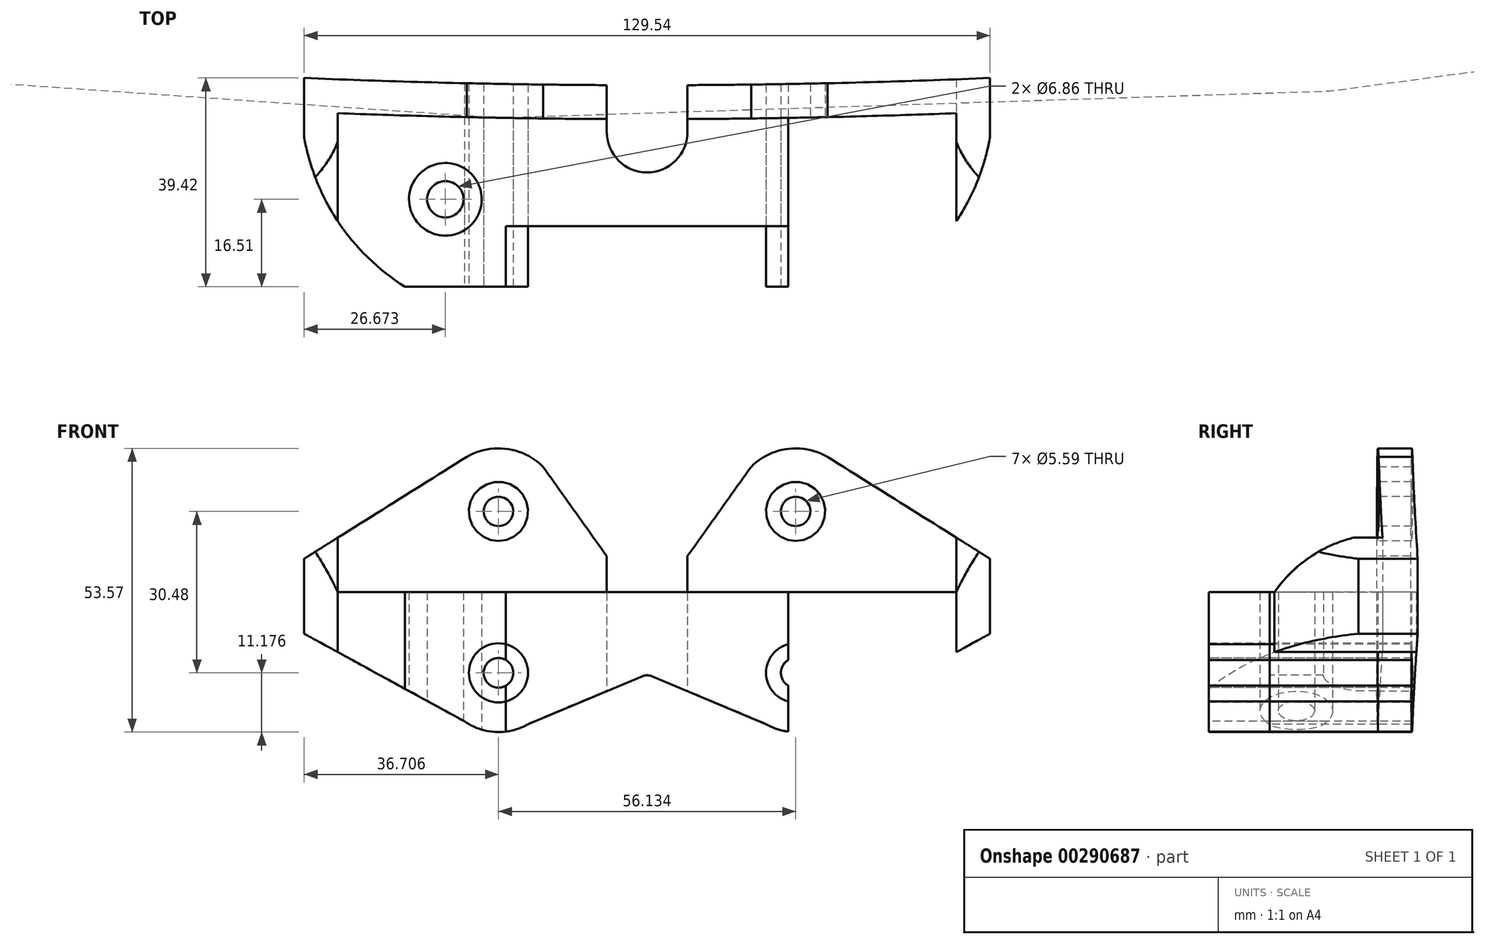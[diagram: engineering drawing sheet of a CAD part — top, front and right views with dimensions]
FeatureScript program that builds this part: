
annotation { "Feature Type Name" : "Feature", "Feature Type Description" : "" }
export const myFeature = defineFeature(function(context is Context, id is Id, definition is map)
    precondition{}
    {
        {
            var Q0;
            Q0=qCreatedBy(makeId("Top.planeOp"),FACE);
            var sketch = newSketch(context, id + "F0", { "sketchPlane" : qUnion([Q0])});
            skLineSegment(sketch, "E0", {"start": v(-442.16, 137.19) * mm, "end": v(-442.16, -137.19) * mm, "construction": true});
            skLineSegment(sketch, "E1.bottom", {"start": v(-353.26, -20.32) * mm, "end": v(-531.06, -20.32) * mm});
            skLineSegment(sketch, "E1.top", {"start": v(-353.26, 20.32) * mm, "end": v(-531.06, 20.32) * mm});
            skLineSegment(sketch, "E1.left", {"start": v(-353.26, -20.32) * mm, "end": v(-353.26, 20.32) * mm});
            skLineSegment(sketch, "E1.right", {"start": v(-531.06, -20.32) * mm, "end": v(-531.06, 20.32) * mm});
            skPoint(sketch, "E1.middle", {"position": v(-442.16, 0) * mm});
            skPoint(sketch, "E1.middle.positionSnap0", {"position": v(-442.16, 0) * mm});
            skPoint(sketch, "E1.centerSnap0", {"position": v(-442.16, 0) * mm});
            skArc(sketch, "E2", {"start": v(-531.06, 20.32) * mm, "mid": v(-442.16, 17.73) * mm, "end": v(-353.26, 20.32) * mm});
            skLineSegment(sketch, "E3", {"start": v(-500.58, -20.32) * mm, "end": v(-500.58, 12.45) * mm});
            skLineSegment(sketch, "E4", {"start": v(-383.74, -20.32) * mm, "end": v(-383.74, 12.45) * mm});
            skArc(sketch, "E5", {"start": v(-500.58, 12.45) * mm, "mid": v(-442.16, 11.33) * mm, "end": v(-383.74, 12.45) * mm});
            skLineSegment(sketch, "E6", {"start": v(-468.83, -20.32) * mm, "end": v(-468.83, -8.9) * mm});
            skLineSegment(sketch, "E7", {"start": v(-468.83, -8.9) * mm, "end": v(-415.49, -8.9) * mm});
            skLineSegment(sketch, "E8", {"start": v(-415.49, -8.9) * mm, "end": v(-415.49, -20.32) * mm});
            skCircle(sketch, "E9", {"center": v(-442.16, 8.89) * mm, "radius": 7.62 * mm});
            skLineSegment(sketch, "E10", {"start": v(-480.26, -3.81) * mm, "end": v(-404.06, -3.81) * mm, "construction": true});
            skCircle(sketch, "E11", {"center": v(-480.26, -3.81) * mm, "radius": 3.43 * mm});
            skCircle(sketch, "E12", {"center": v(-404.06, -3.81) * mm, "radius": 3.43 * mm});
            skLineSegment(sketch, "E13", {"start": v(-434.54, 20.32) * mm, "end": v(-434.54, 8.89) * mm});
            skLineSegment(sketch, "E14", {"start": v(-449.78, 20.32) * mm, "end": v(-449.78, 8.89) * mm});
            skCircle(sketch, "E15", {"center": v(-480.26, -3.81) * mm, "radius": 6.86 * mm});
            skCircle(sketch, "E16", {"center": v(-404.06, -3.81) * mm, "radius": 6.86 * mm});
            skSolve(sketch);
        }
        {
            var Q0;
            Q0=sQuery(id+"F0.wireOp",EDGE,"E1.bottom");
            var Q1;
            Q1=qCreatedBy(makeId("Front.planeOp"),FACE);
            cPlane(context, id + "F1", {"entities" : qUnion([Q0, Q1]), "cplaneType" : CPlaneType.LINE_ANGLE, "offset" : 25.4 * mm, "angle" : 0 * degree, "width" : 152.4 * mm, "height" : 152.4 * mm});
        }
        {
            var Q0;
            Q0=qCreatedBy(id+"F1.planeOp",FACE);
            var sketch = newSketch(context, id + "F2", { "sketchPlane" : qUnion([Q0])});
            skLineSegment(sketch, "E17", {"start": v(531.06, 0) * mm, "end": v(353.26, 0) * mm, "construction": true});
            skLineSegment(sketch, "E18.bottom", {"start": v(414.09, 44.2) * mm, "end": v(470.22, 44.2) * mm, "construction": true});
            skLineSegment(sketch, "E18.top", {"start": v(414.09, 13.72) * mm, "end": v(470.22, 13.72) * mm, "construction": true});
            skLineSegment(sketch, "E18.left", {"start": v(414.09, 44.2) * mm, "end": v(414.09, 13.72) * mm, "construction": true});
            skLineSegment(sketch, "E18.right", {"start": v(470.22, 44.2) * mm, "end": v(470.22, 13.72) * mm, "construction": true});
            skPoint(sketch, "E18.middle", {"position": v(442.16, 28.96) * mm});
            skLineSegment(sketch, "E19", {"start": v(407.26, 28.96) * mm, "end": v(380.42, 28.96) * mm, "construction": true});
            skCircle(sketch, "E20", {"center": v(414.09, 13.72) * mm, "radius": 2.8 * mm});
            skCircle(sketch, "E21", {"center": v(414.09, 44.2) * mm, "radius": 2.8 * mm});
            skCircle(sketch, "E22", {"center": v(470.22, 44.2) * mm, "radius": 2.8 * mm});
            skCircle(sketch, "E23", {"center": v(470.22, 13.72) * mm, "radius": 2.8 * mm});
            skCircle(sketch, "E24", {"center": v(470.22, 13.72) * mm, "radius": 5.59 * mm});
            skCircle(sketch, "E25", {"center": v(470.22, 44.2) * mm, "radius": 5.59 * mm});
            skCircle(sketch, "E26", {"center": v(414.09, 44.2) * mm, "radius": 5.59 * mm});
            skCircle(sketch, "E27", {"center": v(414.09, 13.72) * mm, "radius": 5.59 * mm});
            skLineSegment(sketch, "E28", {"start": v(531.06, 0) * mm, "end": v(531.06, 80.01) * mm, "construction": true});
            skSolve(sketch);
        }
        {
            var Q0;
            {var subQ2=sQuery(id+"F0.wireOp",EDGE,"E1.right");Q0=makeQuery(id+"F0.imprint","IMPRINT",FACE,{"disambiguationData":[TD([[makeQuery(id+"F0.imprint","IMPRINT",EDGE,{"derivedFrom":subQ2}),-1.0]])]});}
            var Q1;
            {var subQ2=sQuery(id+"F0.wireOp",EDGE,"E1.left");Q1=makeQuery(id+"F0.imprint","IMPRINT",FACE,{"disambiguationData":[TD([[makeQuery(id+"F0.imprint","IMPRINT",EDGE,{"derivedFrom":subQ2}),1.0]])]});}
            var Q2;
            Q2=sQuery(id+"F2.wireOp",VERTEX,"E28.end");
            extrude(context, id + "F3", {"entities" : qUnion([Q0, Q1]), "endBound" : BoundingType.UP_TO_VERTEX, "endBoundEntityVertex" : qUnion([Q2]), "depth" : 25.4 * mm});
        }
        {
            var Q0;
            {var subQ10=sQuery(id+"F0.wireOp",EDGE,"E3");Q0=makeQuery(id+"F0.imprint","IMPRINT",FACE,{"disambiguationData":[TD([[makeQuery(id+"F0.imprint","IMPRINT",EDGE,{"derivedFrom":subQ10}),-1.0]])]});}
            var Q1;
            Q1=makeQuery(id+"F0.imprint","IMPRINT",FACE,{"disambiguationData":[TD([[makeQuery(id+"F0.imprint","IMPRINT",EDGE,{"derivedFrom":sQuery(id+"F0.wireOp",EDGE,"E11")}),-1.0]])]});
            var Q2;
            Q2=makeQuery(id+"F0.imprint","IMPRINT",FACE,{"disambiguationData":[TD([[makeQuery(id+"F0.imprint","IMPRINT",EDGE,{"derivedFrom":sQuery(id+"F0.wireOp",EDGE,"E12")}),-1.0]])]});
            var Q3;
            Q3=sQuery(id+"F2.wireOp",VERTEX,"E19.start");
            extrude(context, id + "F4", {"entities" : qUnion([Q0, Q1, Q2]), "endBound" : BoundingType.UP_TO_VERTEX, "endBoundEntityVertex" : qUnion([Q3]), "depth" : 25.4 * mm});
        }
        {
            var Q0;
            Q0=makeQuery(id+"F2.imprint","IMPRINT",FACE,{"disambiguationData":[TD([[makeQuery(id+"F2.imprint","IMPRINT",EDGE,{"derivedFrom":sQuery(id+"F2.wireOp",EDGE,"E22")}),1.0]])]});
            var Q1;
            Q1=makeQuery(id+"F2.imprint","IMPRINT",FACE,{"disambiguationData":[TD([[makeQuery(id+"F2.imprint","IMPRINT",EDGE,{"derivedFrom":sQuery(id+"F2.wireOp",EDGE,"E23")}),1.0]])]});
            var Q2;
            Q2=makeQuery(id+"F2.imprint","IMPRINT",FACE,{"disambiguationData":[TD([[makeQuery(id+"F2.imprint","IMPRINT",EDGE,{"derivedFrom":sQuery(id+"F2.wireOp",EDGE,"E21")}),1.0]])]});
            var Q3;
            Q3=makeQuery(id+"F2.imprint","IMPRINT",FACE,{"disambiguationData":[TD([[makeQuery(id+"F2.imprint","IMPRINT",EDGE,{"derivedFrom":sQuery(id+"F2.wireOp",EDGE,"E20")}),1.0]])]});
            extrude(context, id + "F5", {"entities" : qUnion([Q0, Q1, Q2, Q3]), "operationType" : NewBodyOperationType.REMOVE, "endBound" : BoundingType.THROUGH_ALL, "depth" : 25.4 * mm});
        }
        {
            var Q0;
            Q0=makeQuery(id+"F2.imprint","IMPRINT",FACE,{"disambiguationData":[TD([[makeQuery(id+"F2.imprint","IMPRINT",EDGE,{"derivedFrom":sQuery(id+"F2.wireOp",EDGE,"E22")}),-1.0]])]});
            var Q1;
            Q1=makeQuery(id+"F2.imprint","IMPRINT",FACE,{"disambiguationData":[TD([[makeQuery(id+"F2.imprint","IMPRINT",EDGE,{"derivedFrom":sQuery(id+"F2.wireOp",EDGE,"E21")}),-1.0]])]});
            var Q2;
            {var subQ0=sQuery(id+"F0.wireOp",EDGE,"E2");Q2=makeQuery(id+"F3.opExtrude","SWEPT_FACE",FACE,{"disambiguationData":[OSD([subQ0]),TDD([makeQuery(id+"F0.imprint","IMPRINT",EDGE,{"disambiguationData":[TD([[makeQuery(id+"F0.imprint","INTERSECT",VERTEX,{"derivedFrom":[subQ0,sQuery(id+"F0.wireOp",EDGE,"E14")]}),1.0]])],"derivedFrom":subQ0})])]});}
            var Q3;
            {var subQ0=sQuery(id+"F0.wireOp",EDGE,"E5");Q3=makeQuery(id+"F3.opExtrude","SWEPT_FACE",FACE,{"disambiguationData":[OSD([subQ0]),TDD([makeQuery(id+"F0.imprint","IMPRINT",EDGE,{"disambiguationData":[TD([[makeQuery(id+"F0.imprint","INTERSECT",VERTEX,{"derivedFrom":[sQuery(id+"F0.wireOp",EDGE,"E3"),subQ0]}),-1.0]])],"derivedFrom":subQ0})])]});}
            extrude(context, id + "F6", {"entities" : qUnion([Q0, Q1]), "endBound" : BoundingType.UP_TO_SURFACE, "endBoundEntityFace" : qUnion([Q2]), "depth" : 25.4 * mm, "hasSecondDirection" : true, "secondDirectionBound" : SecondDirectionBoundingType.UP_TO_SURFACE, "secondDirectionOppositeDirection" : false, "secondDirectionBoundEntityFace" : qUnion([Q3]), "secondDirectionDepth" : 25.4 * mm});
        }
        {
            var Q0;
            Q0=makeQuery(id+"F2.imprint","IMPRINT",FACE,{"disambiguationData":[TD([[makeQuery(id+"F2.imprint","IMPRINT",EDGE,{"derivedFrom":sQuery(id+"F2.wireOp",EDGE,"E23")}),-1.0]])]});
            var Q1;
            Q1=makeQuery(id+"F2.imprint","IMPRINT",FACE,{"disambiguationData":[TD([[makeQuery(id+"F2.imprint","IMPRINT",EDGE,{"derivedFrom":sQuery(id+"F2.wireOp",EDGE,"E20")}),-1.0]])]});
            var Q2;
            {var subQ0=sQuery(id+"F0.wireOp",EDGE,"E2");Q2=makeQuery(id+"F3.opExtrude","SWEPT_FACE",FACE,{"disambiguationData":[OSD([subQ0]),TDD([makeQuery(id+"F0.imprint","IMPRINT",EDGE,{"disambiguationData":[TD([[makeQuery(id+"F0.imprint","INTERSECT",VERTEX,{"derivedFrom":[subQ0,sQuery(id+"F0.wireOp",EDGE,"E14")]}),1.0]])],"derivedFrom":subQ0})])]});}
            extrude(context, id + "F7", {"entities" : qUnion([Q0, Q1]), "endBound" : BoundingType.UP_TO_SURFACE, "endBoundEntityFace" : qUnion([Q2]), "depth" : 25.4 * mm});
        }
        {
            var Q0;
            Q0=makeQuery(id+"F0.imprint","IMPRINT",FACE,{"disambiguationData":[TD([[makeQuery(id+"F0.imprint","IMPRINT",EDGE,{"derivedFrom":sQuery(id+"F0.wireOp",EDGE,"E11")}),-1.0]])]});
            var Q1;
            Q1=makeQuery(id+"F0.imprint","IMPRINT",FACE,{"disambiguationData":[TD([[makeQuery(id+"F0.imprint","IMPRINT",EDGE,{"derivedFrom":sQuery(id+"F0.wireOp",EDGE,"E12")}),-1.0]])]});
            var Q2;
            Q2=sQuery(id+"F2.wireOp",VERTEX,"E19.start");
            extrude(context, id + "F8", {"entities" : qUnion([Q0, Q1]), "endBound" : BoundingType.UP_TO_VERTEX, "endBoundEntityVertex" : qUnion([Q2]), "depth" : 25.4 * mm});
        }
        {
            var Q0;
            {var subQ0=sQuery(id+"F0.wireOp",EDGE,"E1.bottom");Q0=makeQuery(id+"F4.opExtrude","SWEPT_FACE",FACE,{"disambiguationData":[OSD([subQ0]),TDD([makeQuery(id+"F0.imprint","IMPRINT",EDGE,{"disambiguationData":[TD([[makeQuery(id+"F0.imprint","INTERSECT",VERTEX,{"derivedFrom":[subQ0,sQuery(id+"F0.wireOp",EDGE,"E4")]}),-1.0]])],"derivedFrom":subQ0})])]});}
            var sketch = newSketch(context, id + "F9", { "sketchPlane" : qUnion([Q0])});
            skCircle(sketch, "E29", {"center": v(-442.16, 10.71) * mm, "radius": 2.54 * mm});
            skLineSegment(sketch, "E30", {"start": v(-441.17, 13.05) * mm, "end": v(-419.68, 4.03) * mm});
            skLineSegment(sketch, "E31", {"start": v(-434.54, 35.74) * mm, "end": v(-442.16, 35.74) * mm});
            skLineSegment(sketch, "E32", {"start": v(-442.16, -10.57) * mm, "end": v(-442.16, 53.1) * mm});
            skLineSegment(sketch, "E33", {"start": v(-434.54, 35.74) * mm, "end": v(-422.51, 52.62) * mm});
            skArc(sketch, "E34", {"start": v(-408.1, 54.49) * mm, "mid": v(-415.62, 56) * mm, "end": v(-422.51, 52.62) * mm});
            skLineSegment(sketch, "E35", {"start": v(-377.39, 35.27) * mm, "end": v(-377.39, 21.1) * mm});
            skLineSegment(sketch, "E36", {"start": v(-377.39, 21.1) * mm, "end": v(-407.68, 4.56) * mm});
            skArc(sketch, "E37", {"start": v(-419.68, 4.03) * mm, "mid": v(-413.6, 2.55) * mm, "end": v(-407.68, 4.56) * mm});
            skLineSegment(sketch, "E38", {"start": v(-377.39, 35.27) * mm, "end": v(-408.1, 54.49) * mm});
            skLineSegment(sketch, "E39.MirrorCS", {"start": v(-449.78, 35.74) * mm, "end": v(-442.16, 35.74) * mm});
            skLineSegment(sketch, "E40.MirrorCS", {"start": v(-449.78, 35.74) * mm, "end": v(-461.8, 52.62) * mm});
            skArc(sketch, "E41.MirrorCS", {"start": v(-476.22, 54.49) * mm, "mid": v(-468.7, 56) * mm, "end": v(-461.8, 52.62) * mm});
            skLineSegment(sketch, "E42.MirrorCS", {"start": v(-506.93, 35.27) * mm, "end": v(-476.22, 54.49) * mm});
            skLineSegment(sketch, "E43.MirrorCS", {"start": v(-506.93, 35.27) * mm, "end": v(-506.93, 21.1) * mm});
            skLineSegment(sketch, "E44.MirrorCS", {"start": v(-506.93, 21.1) * mm, "end": v(-476.64, 4.56) * mm});
            skArc(sketch, "E45.MirrorCS", {"start": v(-464.63, 4.03) * mm, "mid": v(-470.71, 2.55) * mm, "end": v(-476.64, 4.56) * mm});
            skLineSegment(sketch, "E46.MirrorCS", {"start": v(-443.14, 13.05) * mm, "end": v(-464.63, 4.03) * mm});
            skLineSegment(sketch, "E47", {"start": v(-414.09, 44.2) * mm, "end": v(-422.51, 52.62) * mm, "construction": true});
            skLineSegment(sketch, "E48", {"start": v(-414.09, 52.62) * mm, "end": v(-414.09, 44.2) * mm, "construction": true});
            skLineSegment(sketch, "E49", {"start": v(-414.09, 13.72) * mm, "end": v(-407.68, 4.56) * mm, "construction": true});
            skLineSegment(sketch, "E50", {"start": v(-414.09, 6.12) * mm, "end": v(-414.09, 13.72) * mm, "construction": true});
            skLineSegment(sketch, "E51", {"start": v(-419.68, 4.03) * mm, "end": v(-414.09, 13.72) * mm, "construction": true});
            skSolve(sketch);
        }
        {
            var Q0;
            {var subQ0=sQuery(id+"F9.wireOp",EDGE,"E39.MirrorCS");Q0=makeQuery(id+"F9.imprint","IMPRINT",FACE,{"disambiguationData":[TD([[makeQuery(id+"F9.imprint","IMPRINT",EDGE,{"derivedFrom":subQ0}),-1.0]])]});}
            var Q1;
            {var subQ0=sQuery(id+"F2.wireOp",EDGE,"E20");var subQ1=makeQuery(id+"F5.boolean.opBoolean","COPY",EDGE,{"derivedFrom":makeQuery(id+"F5.opExtrude","CAP_EDGE",EDGE,{"disambiguationData":[OSD([subQ0])],"isStart":true})});Q1=makeQuery(id+"F9.imprint","IMPRINT",FACE,{"disambiguationData":[TD([[makeQuery(id+"F9.imprint","IMPRINT",EDGE,{"derivedFrom":subQ1}),1.0]])]});}
            var Q2;
            {var subQ1=sQuery(id+"F9.wireOp",EDGE,"E30");Q2=makeQuery(id+"F9.imprint","IMPRINT",FACE,{"disambiguationData":[TD([[makeQuery(id+"F9.imprint","IMPRINT",EDGE,{"derivedFrom":subQ1}),1.0]])]});}
            extrude(context, id + "F10", {"entities" : qUnion([Q0, Q1, Q2]), "operationType" : NewBodyOperationType.INTERSECT, "endBound" : BoundingType.THROUGH_ALL, "oppositeDirection" : true, "depth" : 25.4 * mm});
        }
        {
            var Q0;
            Q0=qCreatedBy(makeId("Top.planeOp"),FACE);
            var sketch = newSketch(context, id + "F11", { "sketchPlane" : qUnion([Q0])});
            skLineSegment(sketch, "E52", {"start": v(-404.06, -3.81) * mm, "end": v(-396.44, -3.81) * mm, "construction": true});
            skLineSegment(sketch, "E53", {"start": v(-396.44, -3.81) * mm, "end": v(-396.44, -20.32) * mm, "construction": true});
            skArc(sketch, "E54", {"start": v(-396.44, -20.32) * mm, "mid": v(-381.67, -4.46) * mm, "end": v(-376.75, 16.64) * mm});
            skLineSegment(sketch, "E55", {"start": v(-442.16, 32.9) * mm, "end": v(-442.16, -20.32) * mm});
            skLineSegment(sketch, "E56", {"start": v(-376.75, 16.64) * mm, "end": v(-376.9, 21.7) * mm});
            skLineSegment(sketch, "E57", {"start": v(-376.9, 21.7) * mm, "end": v(-442.16, 21.7) * mm});
            skLineSegment(sketch, "E58", {"start": v(-396.44, -20.32) * mm, "end": v(-442.16, -20.32) * mm});
            skLineSegment(sketch, "E59.MirrorCS", {"start": v(-487.88, -20.32) * mm, "end": v(-442.16, -20.32) * mm});
            skLineSegment(sketch, "E60.MirrorCS", {"start": v(-507.41, 21.7) * mm, "end": v(-442.16, 21.7) * mm});
            skLineSegment(sketch, "E61.MirrorCS", {"start": v(-507.57, 16.64) * mm, "end": v(-507.41, 21.7) * mm});
            skLineSegment(sketch, "E62.MirrorCS", {"start": v(-480.26, -3.81) * mm, "end": v(-487.88, -3.81) * mm, "construction": true});
            skLineSegment(sketch, "E63.MirrorCS", {"start": v(-487.88, -3.81) * mm, "end": v(-487.88, -20.32) * mm, "construction": true});
            skArc(sketch, "E64.MirrorCS", {"start": v(-487.88, -20.32) * mm, "mid": v(-502.65, -4.46) * mm, "end": v(-507.57, 16.64) * mm});
            skSolve(sketch);
        }
        {
            var Q0;
            Q0=makeQuery(id+"F11.imprint","IMPRINT",FACE,{"disambiguationData":[TD([[makeQuery(id+"F11.imprint","IMPRINT",EDGE,{"derivedFrom":sQuery(id+"F11.wireOp",EDGE,"E54")}),1.0]])]});
            var Q1;
            {var subQ0=sQuery(id+"F11.wireOp",EDGE,"E59.MirrorCS");Q1=makeQuery(id+"F11.imprint","IMPRINT",FACE,{"disambiguationData":[TD([[makeQuery(id+"F11.imprint","IMPRINT",EDGE,{"derivedFrom":subQ0}),1.0]])]});}
            extrude(context, id + "F12", {"entities" : qUnion([Q0, Q1]), "operationType" : NewBodyOperationType.INTERSECT, "endBound" : BoundingType.THROUGH_ALL, "depth" : 25.4 * mm});
        }
        {
            var Q0;
            Q0=makeQuery(id+"F3.opExtrude","SWEPT_FACE",FACE,{"disambiguationData":[OSD([sQuery(id+"F0.wireOp",EDGE,"E3")])]});
            var sketch = newSketch(context, id + "F13", { "sketchPlane" : qUnion([Q0])});
            skArc(sketch, "E65", {"start": v(7.03, 39.24) * mm, "mid": v(-1.4, 35.47) * mm, "end": v(-7.94, 28.96) * mm});
            skSolve(sketch);
        }
        {
            var Q0;
            {var subQ0=sQuery(id+"F13.wireOp",EDGE,"E65");Q0=makeQuery(id+"F13.imprint","IMPRINT",FACE,{"disambiguationData":[TD([[makeQuery(id+"F13.imprint","IMPRINT",EDGE,{"derivedFrom":subQ0}),-1.0]])]});}
            extrude(context, id + "F14", {"entities" : qUnion([Q0]), "operationType" : NewBodyOperationType.REMOVE, "oppositeDirection" : true, "depth" : 25.4 * mm, "hasSecondDirection" : true, "secondDirectionOppositeDirection" : false, "secondDirectionDepth" : 138.68 * mm});
        }
    });
